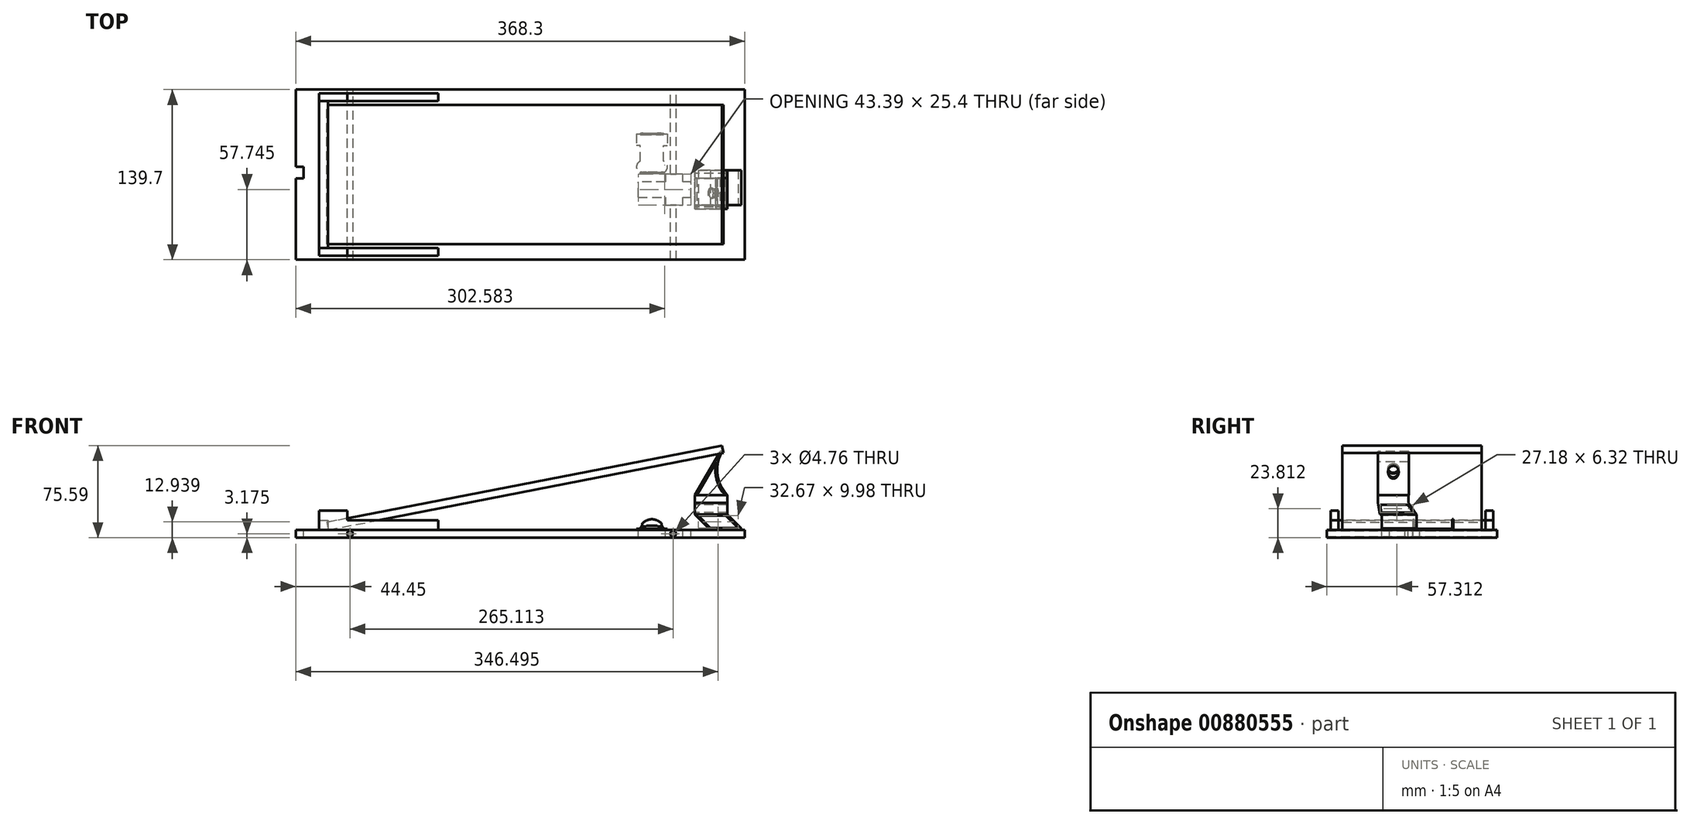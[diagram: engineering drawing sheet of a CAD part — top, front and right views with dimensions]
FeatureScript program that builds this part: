
annotation { "Feature Type Name" : "Feature", "Feature Type Description" : "" }
export const myFeature = defineFeature(function(context is Context, id is Id, definition is map)
    precondition{}
    {
        {
            var Q0;
            Q0=qCreatedBy(makeId("Front.planeOp"),FACE);
            var sketch = newSketch(context, id + "F0", { "sketchPlane" : qUnion([Q0])});
            skLineSegment(sketch, "E0.bottom", {"start": v(0, 0) * mm, "end": v(-368.3, 0) * mm});
            skLineSegment(sketch, "E0.top", {"start": v(0, -6.35) * mm, "end": v(-368.3, -6.35) * mm});
            skLineSegment(sketch, "E0.left", {"start": v(0, 0) * mm, "end": v(0, -6.35) * mm});
            skLineSegment(sketch, "E0.right", {"start": v(-368.3, 0) * mm, "end": v(-368.3, -6.35) * mm});
            skLineSegment(sketch, "E1", {"start": v(0, -60.14) * mm, "end": v(-58.74, -60.14) * mm});
            skCircle(sketch, "E2", {"center": v(-58.74, -3.17) * mm, "radius": 2.38 * mm});
            skPoint(sketch, "E2.centerSnap0", {"position": v(0, -3.17) * mm});
            skLineSegment(sketch, "E3", {"start": v(-368.3, -60.14) * mm, "end": v(-323.85, -60.14) * mm});
            skCircle(sketch, "E4", {"center": v(-323.85, -3.17) * mm, "radius": 2.38 * mm});
            skPoint(sketch, "E4.centerSnap0", {"position": v(-368.3, -3.18) * mm});
            skLineSegment(sketch, "E5", {"start": v(-368.3, 20.18) * mm, "end": v(-342.9, 20.18) * mm});
            skLineSegment(sketch, "E6", {"start": v(-341.56, 0) * mm, "end": v(-17.43, 63) * mm});
            skLineSegment(sketch, "E7", {"start": v(-17.43, 63) * mm, "end": v(-18.64, 69.24) * mm});
            skLineSegment(sketch, "E8", {"start": v(-18.64, 69.24) * mm, "end": v(-342.77, 6.23) * mm});
            skLineSegment(sketch, "E9", {"start": v(-342.77, 6.23) * mm, "end": v(-341.56, 0) * mm});
            skSolve(sketch);
        }
        {
            var Q0;
            Q0=makeQuery(id+"F0.imprint","IMPRINT",FACE,{"disambiguationData":[TD([[makeQuery(id+"F0.imprint","IMPRINT",EDGE,{"derivedFrom":sQuery(id+"F0.wireOp",EDGE,"E0.bottom")}),1.0]])]});
            extrude(context, id + "F1", {"entities" : qUnion([Q0]), "depth" : 139.7 * mm, "offsetDistance" : 25.4 * mm});
        }
        {
            var Q0;
            Q0=makeQuery(id+"F1.opExtrude","SWEPT_FACE",FACE,{"disambiguationData":[OSD([sQuery(id+"F0.wireOp",EDGE,"E0.bottom")])]});
            var sketch = newSketch(context, id + "F2", { "sketchPlane" : qUnion([Q0])});
            skLineSegment(sketch, "E10", {"start": v(-445.44, 0) * mm, "end": v(-445.44, -63.5) * mm});
            skLineSegment(sketch, "E11", {"start": v(-368.3, -63.5) * mm, "end": v(-361.95, -63.5) * mm});
            skPoint(sketch, "E11.startSnap0", {"position": v(-368.3, -69.85) * mm});
            skLineSegment(sketch, "E12", {"start": v(-361.95, -63.5) * mm, "end": v(-361.95, -73.02) * mm});
            skLineSegment(sketch, "E13", {"start": v(-361.95, -73.02) * mm, "end": v(-368.3, -73.02) * mm});
            skLineSegment(sketch, "E14", {"start": v(-368.3, 0) * mm, "end": v(-88.9, 0) * mm});
            skLineSegment(sketch, "E15", {"start": v(-88.9, 0) * mm, "end": v(-88.9, -36.51) * mm});
            skLineSegment(sketch, "E16", {"start": v(-88.9, -36.51) * mm, "end": v(-63.5, -36.51) * mm});
            skLineSegment(sketch, "E17", {"start": v(-63.5, -36.51) * mm, "end": v(-63.5, -68.26) * mm});
            skLineSegment(sketch, "E18", {"start": v(-88.9, -36.51) * mm, "end": v(-88.9, -68.26) * mm});
            skLineSegment(sketch, "E19", {"start": v(-88.9, -68.26) * mm, "end": v(-63.5, -68.26) * mm});
            skLineSegment(sketch, "E20.bottom", {"start": v(-69.85, -68.26) * mm, "end": v(-63.5, -68.26) * mm});
            skLineSegment(sketch, "E20.top", {"start": v(-69.85, -36.51) * mm, "end": v(-63.5, -36.51) * mm});
            skLineSegment(sketch, "E20.left", {"start": v(-69.85, -68.26) * mm, "end": v(-69.85, -36.51) * mm});
            skLineSegment(sketch, "E20.right", {"start": v(-63.5, -68.26) * mm, "end": v(-63.5, -36.51) * mm});
            skLineSegment(sketch, "E21.bottom", {"start": v(-88.9, -36.51) * mm, "end": v(-82.55, -36.51) * mm});
            skLineSegment(sketch, "E21.top", {"start": v(-88.9, -68.26) * mm, "end": v(-82.55, -68.26) * mm});
            skLineSegment(sketch, "E21.right", {"start": v(-82.55, -36.51) * mm, "end": v(-82.55, -68.26) * mm});
            skLineSegment(sketch, "E22", {"start": v(-97.35, -52.39) * mm, "end": v(-97.35, -46.04) * mm});
            skPoint(sketch, "E22.startSnap0", {"position": v(-88.9, -52.39) * mm});
            skLineSegment(sketch, "E23", {"start": v(-97.35, -52.39) * mm, "end": v(-97.35, -58.74) * mm});
            skPoint(sketch, "E24.firstSnap0", {"position": v(-85.72, -36.51) * mm});
            skLineSegment(sketch, "E24.bottom", {"start": v(-85.72, -46.04) * mm, "end": v(-88.9, -46.04) * mm});
            skLineSegment(sketch, "E24.top", {"start": v(-85.72, -58.74) * mm, "end": v(-88.9, -58.74) * mm});
            skLineSegment(sketch, "E24.left", {"start": v(-85.72, -46.04) * mm, "end": v(-85.72, -58.74) * mm});
            skLineSegment(sketch, "E24.right", {"start": v(-88.9, -46.04) * mm, "end": v(-88.9, -58.74) * mm});
            skPoint(sketch, "E25.firstSnap0", {"position": v(-66.67, -36.51) * mm});
            skLineSegment(sketch, "E25.bottom", {"start": v(-66.67, -46.04) * mm, "end": v(-63.5, -46.04) * mm});
            skLineSegment(sketch, "E25.top", {"start": v(-66.67, -58.74) * mm, "end": v(-63.5, -58.74) * mm});
            skLineSegment(sketch, "E25.left", {"start": v(-66.67, -46.04) * mm, "end": v(-66.67, -58.74) * mm});
            skLineSegment(sketch, "E25.right", {"start": v(-63.5, -46.04) * mm, "end": v(-63.5, -58.74) * mm});
            skArc(sketch, "E26", {"start": v(-85.72, -36.51) * mm, "mid": v(-88.87, -41.27) * mm, "end": v(-85.72, -46.04) * mm});
            skArc(sketch, "E27", {"start": v(-85.72, -58.74) * mm, "mid": v(-88.87, -63.5) * mm, "end": v(-85.72, -68.26) * mm});
            skArc(sketch, "E28", {"start": v(-66.67, -46.04) * mm, "mid": v(-63.53, -41.27) * mm, "end": v(-66.67, -36.51) * mm});
            skArc(sketch, "E29", {"start": v(-66.67, -68.26) * mm, "mid": v(-63.53, -63.5) * mm, "end": v(-66.67, -58.74) * mm});
            skLineSegment(sketch, "E30", {"start": v(-368.3, -158.75) * mm, "end": v(-87.41, -158.75) * mm});
            skLineSegment(sketch, "E31", {"start": v(-87.41, -139.7) * mm, "end": v(-87.41, -88.3) * mm});
            skLineSegment(sketch, "E32", {"start": v(-87.41, -88.3) * mm, "end": v(-87.41, -75.6) * mm});
            skLineSegment(sketch, "E33", {"start": v(-87.41, -88.3) * mm, "end": v(-65.19, -88.3) * mm});
            skLineSegment(sketch, "E34", {"start": v(-65.19, -88.3) * mm, "end": v(-65.19, -94.65) * mm});
            skLineSegment(sketch, "E35", {"start": v(-65.19, -94.65) * mm, "end": v(-50.9, -94.65) * mm});
            skLineSegment(sketch, "E36", {"start": v(-50.9, -94.65) * mm, "end": v(-50.9, -88.3) * mm});
            skLineSegment(sketch, "E37", {"start": v(-50.9, -88.3) * mm, "end": v(-44.02, -88.3) * mm});
            skLineSegment(sketch, "E38", {"start": v(-44.02, -88.3) * mm, "end": v(-44.02, -75.6) * mm});
            skLineSegment(sketch, "E39", {"start": v(-44.02, -75.6) * mm, "end": v(-50.9, -75.6) * mm});
            skLineSegment(sketch, "E40", {"start": v(-50.9, -75.6) * mm, "end": v(-50.9, -69.25) * mm});
            skLineSegment(sketch, "E41", {"start": v(-50.9, -69.25) * mm, "end": v(-65.19, -69.25) * mm});
            skLineSegment(sketch, "E42", {"start": v(-65.19, -69.25) * mm, "end": v(-65.19, -75.6) * mm});
            skLineSegment(sketch, "E43", {"start": v(-65.19, -75.6) * mm, "end": v(-87.41, -75.6) * mm});
            skLineSegment(sketch, "E44", {"start": v(-44.02, -88.3) * mm, "end": v(-40.85, -88.3) * mm});
            skLineSegment(sketch, "E45", {"start": v(-40.85, -88.3) * mm, "end": v(-2.75, -88.3) * mm});
            skLineSegment(sketch, "E46", {"start": v(-40.85, -88.3) * mm, "end": v(-40.85, -94.65) * mm});
            skLineSegment(sketch, "E47.bottom", {"start": v(-40.85, -94.65) * mm, "end": v(-2.75, -94.65) * mm});
            skLineSegment(sketch, "E47.top", {"start": v(-40.85, -66.08) * mm, "end": v(-2.75, -66.08) * mm});
            skLineSegment(sketch, "E47.left", {"start": v(-40.85, -94.65) * mm, "end": v(-40.85, -66.08) * mm});
            skLineSegment(sketch, "E47.right", {"start": v(-2.75, -94.65) * mm, "end": v(-2.75, -66.08) * mm});
            skLineSegment(sketch, "E48", {"start": v(-368.3, -150.9) * mm, "end": v(-349.25, -150.9) * mm});
            skLineSegment(sketch, "E49", {"start": v(-356.96, -139.7) * mm, "end": v(-356.96, -136.53) * mm});
            skLineSegment(sketch, "E50", {"start": v(-349.25, -136.53) * mm, "end": v(-349.25, -3.17) * mm});
            skLineSegment(sketch, "E51", {"start": v(-349.25, -136.53) * mm, "end": v(-342.1, -136.53) * mm});
            skLineSegment(sketch, "E52", {"start": v(-349.25, -3.17) * mm, "end": v(-342.1, -3.17) * mm});
            skLineSegment(sketch, "E53", {"start": v(-342.1, -3.17) * mm, "end": v(-342.1, -136.53) * mm});
            skSolve(sketch);
        }
        {
            var Q0;
            {var subQ0=sQuery(id+"F2.wireOp",EDGE,"E11");Q0=makeQuery(id+"F2.imprint","IMPRINT",FACE,{"disambiguationData":[TD([[makeQuery(id+"F2.imprint","IMPRINT",EDGE,{"derivedFrom":subQ0}),-1.0]])]});}
            extrude(context, id + "F3", {"entities" : qUnion([Q0]), "operationType" : NewBodyOperationType.REMOVE, "oppositeDirection" : true, "depth" : 25.4 * mm, "offsetDistance" : 25.4 * mm});
        }
        {
            var Q0;
            {var subQ0=sQuery(id+"F2.wireOp",EDGE,"E21.right");Q0=makeQuery(id+"F2.imprint","IMPRINT",FACE,{"disambiguationData":[TD([[makeQuery(id+"F2.imprint","IMPRINT",EDGE,{"derivedFrom":subQ0}),-1.0]])]});}
            var Q1;
            Q1=makeQuery(id+"F2.imprint","IMPRINT",FACE,{"disambiguationData":[TD([[makeQuery(id+"F2.imprint","IMPRINT",EDGE,{"derivedFrom":sQuery(id+"F2.wireOp",EDGE,"E16")}),-1.0]])]});
            var Q2;
            {var subQ0=sQuery(id+"F2.wireOp",EDGE,"E20.left");Q2=makeQuery(id+"F2.imprint","IMPRINT",FACE,{"disambiguationData":[TD([[makeQuery(id+"F2.imprint","IMPRINT",EDGE,{"derivedFrom":subQ0}),-1.0]])]});}
            extrude(context, id + "F4", {"entities" : qUnion([Q0, Q1, Q2]), "depth" : 0.8 * mm, "offsetDistance" : 25.4 * mm});
        }
        {
            var Q0;
            Q0=makeQuery(id+"F4.opExtrude","CAP_FACE",FACE,{"disambiguationData":[OSD([sQuery(id+"F2.wireOp",EDGE,"E16"),sQuery(id+"F2.wireOp",EDGE,"E19"),sQuery(id+"F2.wireOp",EDGE,"E20.bottom"),sQuery(id+"F2.wireOp",EDGE,"E20.top"),sQuery(id+"F2.wireOp",EDGE,"E21.bottom"),sQuery(id+"F2.wireOp",EDGE,"E21.top"),sQuery(id+"F2.wireOp",EDGE,"E24.left"),sQuery(id+"F2.wireOp",EDGE,"E25.left"),sQuery(id+"F2.wireOp",EDGE,"E26"),sQuery(id+"F2.wireOp",EDGE,"E27"),sQuery(id+"F2.wireOp",EDGE,"E28"),sQuery(id+"F2.wireOp",EDGE,"E29")])],"isStart":false});
            var sketch = newSketch(context, id + "F5", { "sketchPlane" : qUnion([Q0])});
            skLineSegment(sketch, "E54.bottom", {"start": v(-85.72, -46.04) * mm, "end": v(-66.67, -46.04) * mm});
            skLineSegment(sketch, "E54.top", {"start": v(-85.72, -58.74) * mm, "end": v(-66.67, -58.74) * mm});
            skLineSegment(sketch, "E54.left", {"start": v(-85.72, -46.04) * mm, "end": v(-85.72, -58.74) * mm});
            skLineSegment(sketch, "E54.right", {"start": v(-66.67, -46.04) * mm, "end": v(-66.67, -58.74) * mm});
            skSolve(sketch);
        }
        {
            var Q0;
            Q0 = qSketchRegion(id + "F5", true);
            extrude(context, id + "F6", {"entities" : qUnion([Q0]), "operationType" : NewBodyOperationType.ADD, "depth" : 7.94 * mm, "offsetDistance" : 25.4 * mm});
        }
        {
            var Q0;
            Q0=makeQuery(id+"F6.opExtrude","SWEPT_FACE",FACE,{"disambiguationData":[OSD([sQuery(id+"F5.wireOp",EDGE,"E54.bottom")])]});
            var sketch = newSketch(context, id + "F7", { "sketchPlane" : qUnion([Q0])});
            skLineSegment(sketch, "E55", {"start": v(66.67, 8.73) * mm, "end": v(66.67, 0.8) * mm});
            skLineSegment(sketch, "E56", {"start": v(66.67, 0.8) * mm, "end": v(66.67, 0) * mm});
            skLineSegment(sketch, "E57", {"start": v(66.67, 0) * mm, "end": v(68.26, 2.75) * mm});
            skLineSegment(sketch, "E58", {"start": v(68.26, 2.75) * mm, "end": v(71.44, 2.75) * mm});
            skLineSegment(sketch, "E59", {"start": v(76.2, 8.73) * mm, "end": v(76.2, 0) * mm});
            skLineSegment(sketch, "E60", {"start": v(71.44, 2.75) * mm, "end": v(71.83, 3.44) * mm});
            skLineSegment(sketch, "E61", {"start": v(71.83, 3.44) * mm, "end": v(76.2, 3.44) * mm});
            skLineSegment(sketch, "E62", {"start": v(68.26, 2.75) * mm, "end": v(68.26, 5.13) * mm});
            skLineSegment(sketch, "E63.MirrorCS", {"start": v(80.57, 3.44) * mm, "end": v(76.2, 3.44) * mm});
            skLineSegment(sketch, "E64.MirrorCS", {"start": v(80.96, 2.75) * mm, "end": v(80.57, 3.44) * mm});
            skLineSegment(sketch, "E65.MirrorCS", {"start": v(84.14, 2.75) * mm, "end": v(80.96, 2.75) * mm});
            skLineSegment(sketch, "E66.MirrorCS", {"start": v(84.14, 2.75) * mm, "end": v(84.14, 5.13) * mm});
            skLineSegment(sketch, "E67.MirrorCS", {"start": v(85.72, 0) * mm, "end": v(84.14, 2.75) * mm});
            skLineSegment(sketch, "E68", {"start": v(84.93, 1.37) * mm, "end": v(84.59, 1.18) * mm});
            skLineSegment(sketch, "E69", {"start": v(84.59, 1.18) * mm, "end": v(83.68, 2.75) * mm});
            skLineSegment(sketch, "E70", {"start": v(83.68, 2.75) * mm, "end": v(85.27, 0) * mm});
            skLineSegment(sketch, "E71.MirrorCS", {"start": v(84.93, 1.37) * mm, "end": v(85.27, 1.57) * mm});
            skLineSegment(sketch, "E72", {"start": v(85.27, 1.57) * mm, "end": v(84.14, 3.54) * mm});
            skLineSegment(sketch, "E73", {"start": v(84.14, 3.54) * mm, "end": v(85.72, 0.8) * mm});
            skLineSegment(sketch, "E74.MirrorCS", {"start": v(68.72, 2.75) * mm, "end": v(67.13, 0) * mm});
            skLineSegment(sketch, "E75.MirrorCS", {"start": v(68.26, 3.54) * mm, "end": v(66.67, 0.8) * mm});
            skLineSegment(sketch, "E76", {"start": v(89.23, 0) * mm, "end": v(89.23, 8.73) * mm});
            skArc(sketch, "E77", {"start": v(84.14, 5.13) * mm, "mid": v(76.2, 8.73) * mm, "end": v(68.26, 5.13) * mm});
            skSolve(sketch);
        }
        {
            var Q0;
            {var subQ6=sQuery(id+"F7.wireOp",EDGE,"E55");Q0=makeQuery(id+"F7.imprint","IMPRINT",FACE,{"disambiguationData":[TD([[makeQuery(id+"F7.imprint","IMPRINT",EDGE,{"derivedFrom":subQ6}),1.0]])]});}
            var Q1;
            {var subQ1=sQuery(id+"F5.wireOp",EDGE,"E54.bottom");var subQ8=makeQuery(id+"F6.opExtrude","SWEPT_EDGE",EDGE,{"disambiguationData":[OSD([sQuery(id+"F2.wireOp",EDGE,"E26"),subQ1,sQuery(id+"F5.wireOp",EDGE,"E54.left")])]});Q1=makeQuery(id+"F7.imprint","IMPRINT",FACE,{"disambiguationData":[TD([[makeQuery(id+"F7.imprint","IMPRINT",EDGE,{"derivedFrom":subQ8}),-1.0]])]});}
            var Q2;
            {var subQ8=sQuery(id+"F7.wireOp",EDGE,"E63.MirrorCS");Q2=makeQuery(id+"F7.imprint","IMPRINT",FACE,{"disambiguationData":[TD([[makeQuery(id+"F7.imprint","IMPRINT",EDGE,{"derivedFrom":subQ8}),1.0]])]});}
            var Q3;
            {var subQ1=sQuery(id+"F7.wireOp",EDGE,"E60");Q3=makeQuery(id+"F7.imprint","IMPRINT",FACE,{"disambiguationData":[TD([[makeQuery(id+"F7.imprint","IMPRINT",EDGE,{"derivedFrom":subQ1}),-1.0]])]});}
            extrude(context, id + "F8", {"entities" : qUnion([Q0, Q1, Q2, Q3]), "operationType" : NewBodyOperationType.REMOVE, "oppositeDirection" : true, "depth" : 44.45 * mm, "offsetDistance" : 25.4 * mm});
        }
        {
            var Q0;
            Q0=makeQuery(id+"F6.boolean.opBoolean","MERGE",FACE,{"derivedFrom":[makeQuery(id+"F4.opExtrude","SWEPT_FACE",FACE,{"disambiguationData":[OSD([sQuery(id+"F2.wireOp",EDGE,"E25.left")])]}),makeQuery(id+"F6.opExtrude","SWEPT_FACE",FACE,{"disambiguationData":[OSD([sQuery(id+"F5.wireOp",EDGE,"E54.right")])]})]});
            var sketch = newSketch(context, id + "F9", { "sketchPlane" : qUnion([Q0])});
            skLineSegment(sketch, "E78", {"start": v(-58.74, 0.8) * mm, "end": v(-57.94, 0.8) * mm});
            skLineSegment(sketch, "E79", {"start": v(-46.04, 0.8) * mm, "end": v(-46.83, 0.8) * mm});
            skLineSegment(sketch, "E80.bottom", {"start": v(-57.94, 0.8) * mm, "end": v(-46.83, 0.8) * mm});
            skLineSegment(sketch, "E80.top", {"start": v(-57.94, 10.15) * mm, "end": v(-46.83, 10.15) * mm});
            skLineSegment(sketch, "E80.left", {"start": v(-57.94, 0.8) * mm, "end": v(-57.94, 10.15) * mm});
            skLineSegment(sketch, "E80.right", {"start": v(-46.83, 0.8) * mm, "end": v(-46.83, 10.15) * mm});
            skSolve(sketch);
        }
        {
            var Q0;
            Q0=makeQuery(id+"F9.imprint","IMPRINT",FACE,{"disambiguationData":[TD([[makeQuery(id+"F9.imprint","IMPRINT",EDGE,{"derivedFrom":sQuery(id+"F9.wireOp",EDGE,"E80.bottom")}),1.0]])]});
            extrude(context, id + "F10", {"entities" : qUnion([Q0]), "operationType" : NewBodyOperationType.REMOVE, "oppositeDirection" : true, "depth" : 22.35 * mm, "offsetDistance" : 25.4 * mm});
        }
        {
            var Q0;
            Q0=makeQuery(id+"F6.opExtrude","SWEPT_FACE",FACE,{"disambiguationData":[OSD([sQuery(id+"F5.wireOp",EDGE,"E54.top")])]});
            extrude(context, id + "F11", {"entities" : qUnion([Q0]), "operationType" : NewBodyOperationType.ADD, "depth" : 10.16 * mm, "offsetDistance" : 25.4 * mm});
        }
        {
            var Q0;
            Q0=makeQuery(id+"F6.opExtrude","SWEPT_FACE",FACE,{"disambiguationData":[OSD([sQuery(id+"F5.wireOp",EDGE,"E54.bottom")])]});
            extrude(context, id + "F12", {"entities" : qUnion([Q0]), "operationType" : NewBodyOperationType.ADD, "depth" : 10.16 * mm, "offsetDistance" : 25.4 * mm});
        }
        {
            var Q0;
            Q0=makeQuery(id+"F10.boolean.opBoolean","COPY",FACE,{"derivedFrom":makeQuery(id+"F10.opExtrude","SWEPT_FACE",FACE,{"disambiguationData":[OSD([sQuery(id+"F9.wireOp",EDGE,"E80.right")])]})});
            extrude(context, id + "F13", {"entities" : qUnion([Q0]), "operationType" : NewBodyOperationType.REMOVE, "oppositeDirection" : true, "depth" : 9.9 * mm, "offsetDistance" : 25.4 * mm});
        }
        {
            var Q0;
            Q0=makeQuery(id+"F10.boolean.opBoolean","COPY",FACE,{"derivedFrom":makeQuery(id+"F10.opExtrude","SWEPT_FACE",FACE,{"disambiguationData":[OSD([sQuery(id+"F9.wireOp",EDGE,"E80.left")])]})});
            extrude(context, id + "F14", {"entities" : qUnion([Q0]), "operationType" : NewBodyOperationType.REMOVE, "oppositeDirection" : true, "depth" : 9.9 * mm, "offsetDistance" : 25.4 * mm});
        }
        {
            var Q0;
            Q0=makeQuery(id+"F2.imprint","IMPRINT",FACE,{"disambiguationData":[TD([[makeQuery(id+"F2.imprint","IMPRINT",EDGE,{"derivedFrom":sQuery(id+"F2.wireOp",EDGE,"E32")}),-1.0]])]});
            extrude(context, id + "F15", {"entities" : qUnion([Q0]), "operationType" : NewBodyOperationType.REMOVE, "oppositeDirection" : true, "depth" : 6.35 * mm, "offsetDistance" : 25.4 * mm});
        }
        {
            var Q0;
            {var subQ0=sQuery(id+"F2.wireOp",EDGE,"E45");Q0=makeQuery(id+"F2.imprint","IMPRINT",FACE,{"disambiguationData":[TD([[makeQuery(id+"F2.imprint","IMPRINT",EDGE,{"derivedFrom":subQ0}),1.0]])]});}
            var Q1;
            {var subQ0=sQuery(id+"F2.wireOp",EDGE,"E45");Q1=makeQuery(id+"F2.imprint","IMPRINT",FACE,{"disambiguationData":[TD([[makeQuery(id+"F2.imprint","IMPRINT",EDGE,{"derivedFrom":subQ0}),-1.0]])]});}
            extrude(context, id + "F16", {"entities" : qUnion([Q0, Q1]), "depth" : 12.7 * mm, "offsetDistance" : 25.4 * mm});
        }
        {
            var Q0;
            Q0=makeQuery(id+"F16.opExtrude","SWEPT_FACE",FACE,{"disambiguationData":[OSD([sQuery(id+"F2.wireOp",EDGE,"E47.bottom")])]});
            var sketch = newSketch(context, id + "F17", { "sketchPlane" : qUnion([Q0])});
            skLineSegment(sketch, "E81", {"start": v(-2.75, 0) * mm, "end": v(-14.89, 12.14) * mm});
            skLineSegment(sketch, "E82", {"start": v(-2.75, 12.7) * mm, "end": v(-2.75, 0) * mm});
            skLineSegment(sketch, "E83", {"start": v(-5.1, 2.35) * mm, "end": v(-4.54, 2.91) * mm});
            skLineSegment(sketch, "E84.MirrorCS", {"start": v(-5.1, 2.35) * mm, "end": v(-5.66, 1.8) * mm});
            skLineSegment(sketch, "E85", {"start": v(-5.66, 1.8) * mm, "end": v(-15.45, 11.58) * mm});
            skLineSegment(sketch, "E86", {"start": v(-14.89, 12.14) * mm, "end": v(-15.45, 11.58) * mm});
            skLineSegment(sketch, "E87", {"start": v(-15.45, 11.58) * mm, "end": v(-15.45, 11.58) * mm});
            skLineSegment(sketch, "E88", {"start": v(-15.45, 11.58) * mm, "end": v(-3.87, 0) * mm});
            skLineSegment(sketch, "E89", {"start": v(-14.89, 12.14) * mm, "end": v(-13.58, 13.44) * mm});
            skLineSegment(sketch, "E90", {"start": v(-4.54, 2.91) * mm, "end": v(-14.33, 12.7) * mm});
            skLineSegment(sketch, "E91", {"start": v(-14.33, 12.7) * mm, "end": v(-2.75, 1.12) * mm});
            skLineSegment(sketch, "E92", {"start": v(-14.33, 12.7) * mm, "end": v(-40.85, 12.7) * mm});
            skLineSegment(sketch, "E93", {"start": v(-40.85, 12.7) * mm, "end": v(-28.15, 0) * mm});
            skLineSegment(sketch, "E94", {"start": v(-28.15, 0) * mm, "end": v(-3.87, 0) * mm});
            skLineSegment(sketch, "E95", {"start": v(-15.45, 11.58) * mm, "end": v(-39.73, 11.58) * mm});
            skLineSegment(sketch, "E96", {"start": v(-34.5, 6.35) * mm, "end": v(-32.91, 6.35) * mm});
            skLineSegment(sketch, "E97", {"start": v(-32.91, 6.35) * mm, "end": v(-38.14, 11.58) * mm});
            skLineSegment(sketch, "E98", {"start": v(-38.14, 11.58) * mm, "end": v(-26.56, 0) * mm});
            skLineSegment(sketch, "E99", {"start": v(-18.5, 0) * mm, "end": v(-18.5, 1.6) * mm});
            skLineSegment(sketch, "E100", {"start": v(-18.5, 1.6) * mm, "end": v(-28.16, 1.6) * mm});
            skLineSegment(sketch, "E101", {"start": v(-28.16, 1.6) * mm, "end": v(-5.47, 1.6) * mm});
            skSolve(sketch);
        }
        {
            var Q0;
            {var subQ1=sQuery(id+"F17.wireOp",EDGE,"E88");var subQ6=makeQuery(id+"F17.imprint","INTERSECT",VERTEX,{"derivedFrom":[sQuery(id+"F17.wireOp",EDGE,"E84.MirrorCS"),subQ1]});Q0=makeQuery(id+"F17.imprint","IMPRINT",FACE,{"disambiguationData":[TD([[makeQuery(id+"F17.imprint","IMPRINT",EDGE,{"disambiguationData":[TD([[subQ6,-1.0]])],"derivedFrom":subQ1}),-1.0]])]});}
            var Q1;
            {var subQ0=sQuery(id+"F17.wireOp",EDGE,"E82");var subQ1=makeQuery(id+"F16.opExtrude","CAP_EDGE",EDGE,{"disambiguationData":[OSD([sQuery(id+"F2.wireOp",EDGE,"E47.bottom")])],"isStart":false});var subQ2=makeQuery(id+"F17.imprint","INTERSECT",VERTEX,{"derivedFrom":[subQ1,subQ0]});Q1=makeQuery(id+"F17.imprint","IMPRINT",FACE,{"disambiguationData":[TD([[makeQuery(id+"F17.imprint","IMPRINT",EDGE,{"disambiguationData":[TD([[subQ2,-1.0]])],"derivedFrom":subQ0}),-1.0]])]});}
            var Q2;
            {var subQ1=sQuery(id+"F2.wireOp",EDGE,"E47.bottom");var subQ6=makeQuery(id+"F16.opExtrude","SWEPT_EDGE",EDGE,{"disambiguationData":[OSD([subQ1,sQuery(id+"F2.wireOp",EDGE,"E47.left")])]});Q2=makeQuery(id+"F17.imprint","IMPRINT",FACE,{"disambiguationData":[TD([[makeQuery(id+"F17.imprint","IMPRINT",EDGE,{"derivedFrom":subQ6}),1.0]])]});}
            extrude(context, id + "F18", {"entities" : qUnion([Q0, Q1, Q2]), "operationType" : NewBodyOperationType.REMOVE, "oppositeDirection" : true, "depth" : 30.48 * mm, "offsetDistance" : 25.4 * mm});
        }
        {
            var Q0;
            Q0=makeQuery(id+"F16.opExtrude","CAP_FACE",FACE,{"disambiguationData":[OSD([sQuery(id+"F2.wireOp",EDGE,"E47.bottom"),sQuery(id+"F2.wireOp",EDGE,"E47.top"),sQuery(id+"F2.wireOp",EDGE,"E47.left"),sQuery(id+"F2.wireOp",EDGE,"E47.right")])],"isStart":false});
            var sketch = newSketch(context, id + "F19", { "sketchPlane" : qUnion([Q0])});
            skLineSegment(sketch, "E102", {"start": v(-14.33, -66.08) * mm, "end": v(-14.33, -97.83) * mm});
            skLineSegment(sketch, "E103.bottom", {"start": v(-14.33, -97.83) * mm, "end": v(-40.85, -97.83) * mm});
            skLineSegment(sketch, "E103.top", {"start": v(-14.33, -66.08) * mm, "end": v(-40.85, -66.08) * mm});
            skLineSegment(sketch, "E103.left", {"start": v(-14.33, -97.83) * mm, "end": v(-14.33, -66.08) * mm});
            skLineSegment(sketch, "E103.right", {"start": v(-40.85, -97.83) * mm, "end": v(-40.85, -66.08) * mm});
            skSolve(sketch);
        }
        {
            var Q0;
            {var subQ0=sQuery(id+"F19.wireOp",EDGE,"E103.bottom");Q0=makeQuery(id+"F19.imprint","IMPRINT",FACE,{"disambiguationData":[TD([[makeQuery(id+"F19.imprint","IMPRINT",EDGE,{"derivedFrom":subQ0}),-1.0]])]});}
            var Q1;
            {var subQ0=sQuery(id+"F19.wireOp",EDGE,"E103.top");Q1=makeQuery(id+"F19.imprint","IMPRINT",FACE,{"disambiguationData":[TD([[makeQuery(id+"F19.imprint","IMPRINT",EDGE,{"derivedFrom":subQ0}),-1.0]])]});}
            extrude(context, id + "F20", {"entities" : qUnion([Q0, Q1]), "operationType" : NewBodyOperationType.ADD, "depth" : 9.52 * mm, "offsetDistance" : 25.4 * mm});
        }
        {
            var Q0;
            Q0=makeQuery(id+"F20.opExtrude","SWEPT_FACE",FACE,{"disambiguationData":[OSD([sQuery(id+"F19.wireOp",EDGE,"E103.right")])]});
            var sketch = newSketch(context, id + "F21", { "sketchPlane" : qUnion([Q0])});
            skLineSegment(sketch, "E104", {"start": v(97.83, 22.23) * mm, "end": v(96.24, 12.7) * mm});
            skLineSegment(sketch, "E105", {"start": v(96.24, 12.7) * mm, "end": v(66.08, 12.7) * mm});
            skLineSegment(sketch, "E106", {"start": v(66.08, 12.7) * mm, "end": v(72.75, 22.23) * mm});
            skLineSegment(sketch, "E107", {"start": v(72.75, 22.23) * mm, "end": v(97.83, 22.23) * mm});
            skLineSegment(sketch, "E108", {"start": v(96.24, 12.7) * mm, "end": v(94.65, 12.7) * mm});
            skLineSegment(sketch, "E109", {"start": v(94.65, 12.7) * mm, "end": v(96.24, 22.23) * mm});
            skLineSegment(sketch, "E110", {"start": v(66.08, 12.7) * mm, "end": v(67.66, 12.7) * mm});
            skLineSegment(sketch, "E111", {"start": v(66.08, 17.46) * mm, "end": v(67.68, 17.46) * mm});
            skLineSegment(sketch, "E112", {"start": v(67.68, 12.7) * mm, "end": v(74.35, 22.23) * mm});
            skLineSegment(sketch, "E113", {"start": v(74.35, 22.23) * mm, "end": v(74.35, 20.62) * mm});
            skLineSegment(sketch, "E114", {"start": v(73.23, 20.62) * mm, "end": v(95.98, 20.62) * mm});
            skLineSegment(sketch, "E115", {"start": v(94.65, 12.7) * mm, "end": v(94.65, 14.3) * mm});
            skLineSegment(sketch, "E116", {"start": v(94.92, 14.3) * mm, "end": v(68.8, 14.3) * mm});
            skSolve(sketch);
        }
        {
            var Q0;
            {var subQ0=sQuery(id+"F21.wireOp",EDGE,"E114");var subQ2=sQuery(id+"F21.wireOp",EDGE,"E109");var subQ3=makeQuery(id+"F21.imprint","INTERSECT",VERTEX,{"derivedFrom":[subQ2,subQ0]});Q0=makeQuery(id+"F21.imprint","IMPRINT",FACE,{"disambiguationData":[TD([[makeQuery(id+"F21.imprint","IMPRINT",EDGE,{"disambiguationData":[TD([[subQ3,1.0]])],"derivedFrom":subQ2}),1.0]])]});}
            var Q1;
            {var subQ0=sQuery(id+"F21.wireOp",EDGE,"E106");Q1=makeQuery(id+"F21.imprint","IMPRINT",FACE,{"disambiguationData":[TD([[makeQuery(id+"F21.imprint","IMPRINT",EDGE,{"derivedFrom":subQ0}),1.0]])]});}
            var Q2;
            {var subQ0=sQuery(id+"F21.wireOp",EDGE,"E104");Q2=makeQuery(id+"F21.imprint","IMPRINT",FACE,{"disambiguationData":[TD([[makeQuery(id+"F21.imprint","IMPRINT",EDGE,{"derivedFrom":subQ0}),1.0]])]});}
            extrude(context, id + "F22", {"entities" : qUnion([Q0, Q1, Q2]), "operationType" : NewBodyOperationType.REMOVE, "oppositeDirection" : true, "depth" : 31.75 * mm, "offsetDistance" : 25.4 * mm});
        }
        {
            var Q0;
            Q0=makeQuery(id+"F20.opExtrude","CAP_FACE",FACE,{"disambiguationData":[OSD([sQuery(id+"F19.wireOp",EDGE,"E103.bottom"),sQuery(id+"F19.wireOp",EDGE,"E103.top"),sQuery(id+"F19.wireOp",EDGE,"E103.left"),sQuery(id+"F19.wireOp",EDGE,"E103.right")])],"isStart":false});
            extrude(context, id + "F23", {"entities" : qUnion([Q0]), "operationType" : NewBodyOperationType.ADD, "depth" : 6.35 * mm, "offsetDistance" : 25.4 * mm});
        }
        {
            var Q0;
            Q0=makeQuery(id+"F23.opExtrude","SWEPT_FACE",FACE,{"disambiguationData":[OSD([sQuery(id+"F19.wireOp",EDGE,"E103.bottom"),sQuery(id+"F19.wireOp",EDGE,"E103.right"),sQuery(id+"F21.wireOp",EDGE,"E104"),sQuery(id+"F21.wireOp",EDGE,"E107")])]});
            var sketch = newSketch(context, id + "F24", { "sketchPlane" : qUnion([Q0])});
            skLineSegment(sketch, "E117", {"start": v(-40.85, 28.58) * mm, "end": v(-14.33, 28.58) * mm});
            skLineSegment(sketch, "E118", {"start": v(-40.85, 28.58) * mm, "end": v(-20.21, 64.32) * mm});
            skLineSegment(sketch, "E119", {"start": v(-40.85, 38.48) * mm, "end": v(-39.25, 38.48) * mm});
            skLineSegment(sketch, "E120", {"start": v(-39.25, 28.58) * mm, "end": v(-18.61, 64.32) * mm});
            skLineSegment(sketch, "E121", {"start": v(-18.61, 64.32) * mm, "end": v(-20.21, 64.32) * mm});
            skLineSegment(sketch, "E122", {"start": v(-40.85, 28.58) * mm, "end": v(-39.25, 28.58) * mm});
            skArc(sketch, "E123", {"start": v(-18.61, 64.32) * mm, "mid": v(-22.42, 45.73) * mm, "end": v(-14.33, 28.57) * mm});
            skLineSegment(sketch, "E124", {"start": v(-14.33, 33.64) * mm, "end": v(-15.93, 33.64) * mm});
            skArc(sketch, "E125", {"start": v(-20.21, 64.32) * mm, "mid": v(-24.02, 45.73) * mm, "end": v(-15.93, 28.58) * mm});
            skSolve(sketch);
        }
        {
            var Q0;
            {var subQ0=sQuery(id+"F24.wireOp",EDGE,"E118");Q0=makeQuery(id+"F24.imprint","IMPRINT",FACE,{"disambiguationData":[TD([[makeQuery(id+"F24.imprint","IMPRINT",EDGE,{"derivedFrom":subQ0}),-1.0]])]});}
            var Q1;
            {var subQ0=sQuery(id+"F24.wireOp",EDGE,"E121");Q1=makeQuery(id+"F24.imprint","IMPRINT",FACE,{"disambiguationData":[TD([[makeQuery(id+"F24.imprint","IMPRINT",EDGE,{"derivedFrom":subQ0}),1.0]])]});}
            var Q2;
            {var subQ0=sQuery(id+"F24.wireOp",EDGE,"E123");Q2=makeQuery(id+"F24.imprint","IMPRINT",FACE,{"disambiguationData":[TD([[makeQuery(id+"F24.imprint","IMPRINT",EDGE,{"derivedFrom":subQ0}),-1.0]])]});}
            extrude(context, id + "F25", {"entities" : qUnion([Q0, Q1, Q2]), "oppositeDirection" : true, "depth" : 25.4 * mm, "offsetDistance" : 25.4 * mm});
        }
        {
            var Q0;
            Q0=makeQuery(id+"F25.opExtrude","SWEPT_FACE",FACE,{"disambiguationData":[OSD([sQuery(id+"F24.wireOp",EDGE,"E118")])]});
            cPlane(context, id + "F26", {"entities" : qUnion([Q0]), "cplaneType" : CPlaneType.OFFSET, "offset" : 0 * mm, "width" : 152.4 * mm, "height" : 152.4 * mm});
        }
        {
            var Q0;
            Q0=qCreatedBy(id+"F26.planeOp",FACE);
            var sketch = newSketch(context, id + "F27", { "sketchPlane" : qUnion([Q0])});
            skLineSegment(sketch, "E126", {"start": v(72.43, 46.18) * mm, "end": v(72.43, 4.9) * mm});
            skLineSegment(sketch, "E127", {"start": v(72.43, 4.9) * mm, "end": v(97.83, 4.9) * mm});
            skLineSegment(sketch, "E128", {"start": v(85.13, 4.9) * mm, "end": v(85.13, 25.54) * mm});
            skLineSegment(sketch, "E129", {"start": v(85.13, 25.54) * mm, "end": v(85.13, 34.28) * mm});
            skCircle(sketch, "E130", {"center": v(85.13, 29.9) * mm, "radius": 4.37 * mm});
            skSolve(sketch);
        }
        {
            var Q0;
            {var subQ0=sQuery(id+"F27.wireOp",EDGE,"E129");Q0=makeQuery(id+"F27.imprint","IMPRINT",FACE,{"disambiguationData":[TD([[makeQuery(id+"F27.imprint","IMPRINT",EDGE,{"derivedFrom":subQ0}),-1.0]])]});}
            var Q1;
            {var subQ0=sQuery(id+"F27.wireOp",EDGE,"E129");Q1=makeQuery(id+"F27.imprint","IMPRINT",FACE,{"disambiguationData":[TD([[makeQuery(id+"F27.imprint","IMPRINT",EDGE,{"derivedFrom":subQ0}),1.0]])]});}
            extrude(context, id + "F28", {"entities" : qUnion([Q0, Q1]), "operationType" : NewBodyOperationType.REMOVE, "oppositeDirection" : true, "depth" : 25.4 * mm, "offsetDistance" : 25.4 * mm});
        }
        {
            var Q0;
            Q0=makeQuery(id+"F0.imprint","IMPRINT",FACE,{"disambiguationData":[TD([[makeQuery(id+"F0.imprint","IMPRINT",EDGE,{"derivedFrom":sQuery(id+"F0.wireOp",EDGE,"E6")}),1.0]])]});
            extrude(context, id + "F29", {"entities" : qUnion([Q0]), "depth" : 127 * mm, "offsetDistance" : 25.4 * mm});
        }
        {
            var Q0;
            Q0=makeQuery(id+"F29.opExtrude","CAP_FACE",FACE,{"disambiguationData":[OSD([sQuery(id+"F0.wireOp",EDGE,"E6"),sQuery(id+"F0.wireOp",EDGE,"E7"),sQuery(id+"F0.wireOp",EDGE,"E8"),sQuery(id+"F0.wireOp",EDGE,"E9")])],"isStart":true});
            extrude(context, id + "F30", {"entities" : qUnion([Q0]), "operationType" : NewBodyOperationType.REMOVE, "oppositeDirection" : true, "depth" : 12.7 * mm, "offsetDistance" : 25.4 * mm});
        }
        {
            var Q0;
            Q0=makeQuery(id+"F2.imprint","IMPRINT",FACE,{"disambiguationData":[TD([[makeQuery(id+"F2.imprint","IMPRINT",EDGE,{"derivedFrom":sQuery(id+"F2.wireOp",EDGE,"E50")}),-1.0]])]});
            extrude(context, id + "F31", {"entities" : qUnion([Q0]), "depth" : 7.94 * mm, "offsetDistance" : 25.4 * mm});
        }
        {
            var Q0;
            Q0=makeQuery(id+"F31.opExtrude","SWEPT_FACE",FACE,{"disambiguationData":[OSD([sQuery(id+"F2.wireOp",EDGE,"E53")])]});
            var sketch = newSketch(context, id + "F32", { "sketchPlane" : qUnion([Q0])});
            skLineSegment(sketch, "E131.bottom", {"start": v(-3.17, 7.94) * mm, "end": v(-9.52, 7.94) * mm});
            skLineSegment(sketch, "E131.top", {"start": v(-3.17, 0) * mm, "end": v(-9.52, 0) * mm});
            skLineSegment(sketch, "E131.left", {"start": v(-3.17, 7.94) * mm, "end": v(-3.17, 0) * mm});
            skLineSegment(sketch, "E131.right", {"start": v(-9.52, 7.94) * mm, "end": v(-9.52, 0) * mm});
            skLineSegment(sketch, "E132.bottom", {"start": v(-136.53, 7.94) * mm, "end": v(-130.18, 7.94) * mm});
            skLineSegment(sketch, "E132.top", {"start": v(-136.53, 0) * mm, "end": v(-130.18, 0) * mm});
            skLineSegment(sketch, "E132.left", {"start": v(-136.53, 7.94) * mm, "end": v(-136.53, 0) * mm});
            skLineSegment(sketch, "E132.right", {"start": v(-130.18, 7.94) * mm, "end": v(-130.18, 0) * mm});
            skSolve(sketch);
        }
        {
            var Q0;
            Q0=makeQuery(id+"F32.imprint","IMPRINT",FACE,{"disambiguationData":[TD([[makeQuery(id+"F32.imprint","IMPRINT",EDGE,{"derivedFrom":sQuery(id+"F32.wireOp",EDGE,"E131.bottom")}),1.0]])]});
            var Q1;
            Q1=makeQuery(id+"F32.imprint","IMPRINT",FACE,{"disambiguationData":[TD([[makeQuery(id+"F32.imprint","IMPRINT",EDGE,{"derivedFrom":sQuery(id+"F32.wireOp",EDGE,"E132.bottom")}),1.0]])]});
            extrude(context, id + "F33", {"entities" : qUnion([Q0, Q1]), "operationType" : NewBodyOperationType.ADD, "depth" : 90.49 * mm, "offsetDistance" : 25.4 * mm});
        }
        {
            var Q0;
            Q0=makeQuery(id+"F33.boolean.opBoolean","MERGE",FACE,{"derivedFrom":[makeQuery(id+"F31.opExtrude","CAP_FACE",FACE,{"disambiguationData":[OSD([sQuery(id+"F2.wireOp",EDGE,"E50"),sQuery(id+"F2.wireOp",EDGE,"E51"),sQuery(id+"F2.wireOp",EDGE,"E52"),sQuery(id+"F2.wireOp",EDGE,"E53")])],"isStart":false}),makeQuery(id+"F33.opExtrude","SWEPT_FACE",FACE,{"disambiguationData":[OSD([sQuery(id+"F32.wireOp",EDGE,"E131.bottom")])]}),makeQuery(id+"F33.opExtrude","SWEPT_FACE",FACE,{"disambiguationData":[OSD([sQuery(id+"F32.wireOp",EDGE,"E132.bottom")])]})]});
            var sketch = newSketch(context, id + "F34", { "sketchPlane" : qUnion([Q0])});
            skLineSegment(sketch, "E133.bottom", {"start": v(-349.25, -3.17) * mm, "end": v(-326.23, -3.17) * mm});
            skLineSegment(sketch, "E133.top", {"start": v(-349.25, -9.52) * mm, "end": v(-326.23, -9.52) * mm});
            skLineSegment(sketch, "E133.left", {"start": v(-349.25, -3.17) * mm, "end": v(-349.25, -9.52) * mm});
            skLineSegment(sketch, "E133.right", {"start": v(-326.23, -3.17) * mm, "end": v(-326.23, -9.52) * mm});
            skLineSegment(sketch, "E134.bottom", {"start": v(-349.25, -136.53) * mm, "end": v(-326.23, -136.53) * mm});
            skLineSegment(sketch, "E134.top", {"start": v(-349.25, -130.18) * mm, "end": v(-326.23, -130.18) * mm});
            skLineSegment(sketch, "E134.left", {"start": v(-349.25, -136.53) * mm, "end": v(-349.25, -130.18) * mm});
            skLineSegment(sketch, "E134.right", {"start": v(-326.23, -136.53) * mm, "end": v(-326.23, -130.18) * mm});
            skLineSegment(sketch, "E135.bottom", {"start": v(-349.25, -9.52) * mm, "end": v(-342.1, -9.52) * mm});
            skLineSegment(sketch, "E135.top", {"start": v(-349.25, -40.48) * mm, "end": v(-342.1, -40.48) * mm});
            skLineSegment(sketch, "E135.left", {"start": v(-349.25, -9.52) * mm, "end": v(-349.25, -40.48) * mm});
            skLineSegment(sketch, "E135.right", {"start": v(-342.1, -9.52) * mm, "end": v(-342.1, -40.48) * mm});
            skLineSegment(sketch, "E136.bottom", {"start": v(-349.25, -130.18) * mm, "end": v(-342.1, -130.18) * mm});
            skLineSegment(sketch, "E136.top", {"start": v(-349.25, -99.22) * mm, "end": v(-342.1, -99.22) * mm});
            skLineSegment(sketch, "E136.left", {"start": v(-349.25, -130.18) * mm, "end": v(-349.25, -99.22) * mm});
            skLineSegment(sketch, "E136.right", {"start": v(-342.1, -130.18) * mm, "end": v(-342.1, -99.22) * mm});
            skSolve(sketch);
        }
        {
            var Q0;
            Q0=makeQuery(id+"F34.imprint","IMPRINT",FACE,{"disambiguationData":[TD([[makeQuery(id+"F34.imprint","IMPRINT",EDGE,{"derivedFrom":sQuery(id+"F34.wireOp",EDGE,"E135.bottom")}),-1.0]])]});
            var Q1;
            Q1=makeQuery(id+"F34.imprint","IMPRINT",FACE,{"disambiguationData":[TD([[makeQuery(id+"F34.imprint","IMPRINT",EDGE,{"derivedFrom":sQuery(id+"F34.wireOp",EDGE,"E133.bottom")}),-1.0]])]});
            var Q2;
            Q2=makeQuery(id+"F34.imprint","IMPRINT",FACE,{"disambiguationData":[TD([[makeQuery(id+"F34.imprint","IMPRINT",EDGE,{"derivedFrom":sQuery(id+"F34.wireOp",EDGE,"E136.bottom")}),1.0]])]});
            var Q3;
            Q3=makeQuery(id+"F34.imprint","IMPRINT",FACE,{"disambiguationData":[TD([[makeQuery(id+"F34.imprint","IMPRINT",EDGE,{"derivedFrom":sQuery(id+"F34.wireOp",EDGE,"E134.bottom")}),1.0]])]});
            extrude(context, id + "F35", {"entities" : qUnion([Q0, Q1, Q2, Q3]), "operationType" : NewBodyOperationType.ADD, "depth" : 7.94 * mm, "offsetDistance" : 25.4 * mm});
        }
    });
